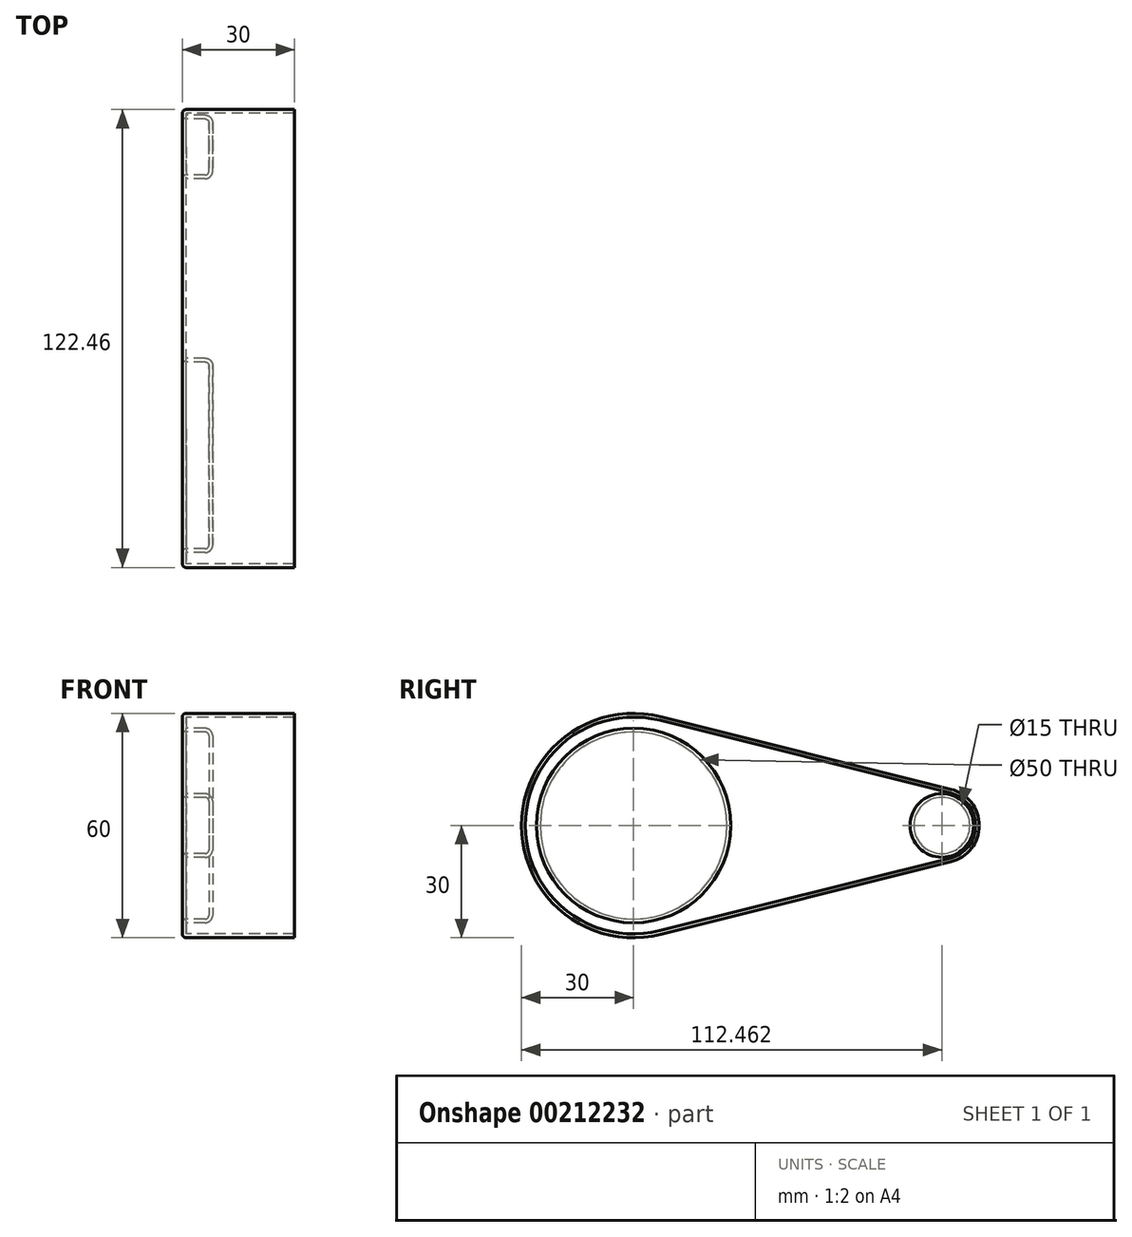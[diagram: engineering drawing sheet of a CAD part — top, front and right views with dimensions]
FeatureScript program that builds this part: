
annotation { "Feature Type Name" : "Feature", "Feature Type Description" : "" }
export const myFeature = defineFeature(function(context is Context, id is Id, definition is map)
    precondition{}
    {
        {
            var Q0;
            Q0=qCreatedBy(makeId("Right.planeOp"),FACE);
            var sketch = newSketch(context, id + "F0", { "sketchPlane" : qUnion([Q0])});
            skCircle(sketch, "E0", {"center": v(0, 0) * mm, "radius": 30 * mm});
            skCircle(sketch, "E1", {"center": v(82.46, 0) * mm, "radius": 10 * mm});
            skLineSegment(sketch, "E2", {"start": v(7.28, 29.1) * mm, "end": v(84.89, 9.7) * mm});
            skLineSegment(sketch, "E3", {"start": v(7.28, -29.1) * mm, "end": v(84.89, -9.7) * mm});
            skSolve(sketch);
        }
        {
            var Q0;
            {var subQ0=sQuery(id+"F0.wireOp",EDGE,"E0");var subQ1=makeQuery(id+"F0.imprint","INTERSECT",VERTEX,{"derivedFrom":[subQ0,sQuery(id+"F0.wireOp",EDGE,"E2")]});Q0=makeQuery(id+"F0.imprint","IMPRINT",FACE,{"disambiguationData":[TD([[makeQuery(id+"F0.imprint","IMPRINT",EDGE,{"disambiguationData":[TD([[subQ1,-1.0]])],"derivedFrom":subQ0}),1.0]])]});}
            var Q1;
            {var subQ0=sQuery(id+"F0.wireOp",EDGE,"E2");Q1=makeQuery(id+"F0.imprint","IMPRINT",FACE,{"disambiguationData":[TD([[makeQuery(id+"F0.imprint","IMPRINT",EDGE,{"derivedFrom":subQ0}),-1.0]])]});}
            var Q2;
            {var subQ0=sQuery(id+"F0.wireOp",EDGE,"E1");var subQ1=makeQuery(id+"F0.imprint","INTERSECT",VERTEX,{"derivedFrom":[subQ0,sQuery(id+"F0.wireOp",EDGE,"E2")]});Q2=makeQuery(id+"F0.imprint","IMPRINT",FACE,{"disambiguationData":[TD([[makeQuery(id+"F0.imprint","IMPRINT",EDGE,{"disambiguationData":[TD([[subQ1,-1.0]])],"derivedFrom":subQ0}),1.0]])]});}
            extrude(context, id + "F1", {"entities" : qUnion([Q0, Q1, Q2]), "depth" : 30 * mm});
        }
        {
            var Q0;
            Q0=makeQuery(id+"F1.opExtrude","CAP_FACE",FACE,{"disambiguationData":[OSD([sQuery(id+"F0.wireOp",EDGE,"E0"),sQuery(id+"F0.wireOp",EDGE,"E1"),sQuery(id+"F0.wireOp",EDGE,"E2"),sQuery(id+"F0.wireOp",EDGE,"E3")])],"isStart":true});
            var sketch = newSketch(context, id + "F2", { "sketchPlane" : qUnion([Q0])});
            skCircle(sketch, "E4", {"center": v(0, 0) * mm, "radius": 25 * mm});
            skCircle(sketch, "E5", {"center": v(-82.46, 0) * mm, "radius": 7.5 * mm});
            skSolve(sketch);
        }
        {
            var Q0;
            Q0=makeQuery(id+"F2.imprint","IMPRINT",FACE,{"disambiguationData":[TD([[makeQuery(id+"F2.imprint","IMPRINT",EDGE,{"derivedFrom":sQuery(id+"F2.wireOp",EDGE,"E4")}),1.0]])]});
            var Q1;
            Q1=makeQuery(id+"F2.imprint","IMPRINT",FACE,{"disambiguationData":[TD([[makeQuery(id+"F2.imprint","IMPRINT",EDGE,{"derivedFrom":sQuery(id+"F2.wireOp",EDGE,"E5")}),1.0]])]});
            var Q2;
            Q2=sQuery(id+"F2.wireOp",EDGE,"E4");
            var Q3;
            Q3=sQuery(id+"F2.wireOp",EDGE,"E5");
            extrude(context, id + "F3", {"entities" : qUnion([Q0, Q1]), "operationType" : NewBodyOperationType.REMOVE, "surfaceEntities" : qUnion([Q2, Q3]), "oppositeDirection" : true, "depth" : 7.1 * mm});
        }
        {
            var Q0;
            Q0=makeQuery(id+"F1.opExtrude","CAP_FACE",FACE,{"disambiguationData":[OSD([sQuery(id+"F0.wireOp",EDGE,"E0"),sQuery(id+"F0.wireOp",EDGE,"E1"),sQuery(id+"F0.wireOp",EDGE,"E2"),sQuery(id+"F0.wireOp",EDGE,"E3")])],"isStart":true});
            var Q1;
            Q1=makeQuery(id+"F3.boolean.opBoolean","COPY",FACE,{"derivedFrom":makeQuery(id+"F3.opExtrude","CAP_FACE",FACE,{"disambiguationData":[OSD([sQuery(id+"F2.wireOp",EDGE,"E4")])],"isStart":false})});
            var Q2;
            Q2=makeQuery(id+"F3.boolean.opBoolean","COPY",FACE,{"derivedFrom":makeQuery(id+"F3.opExtrude","CAP_FACE",FACE,{"disambiguationData":[OSD([sQuery(id+"F2.wireOp",EDGE,"E5")])],"isStart":false})});
            fillet(context, id + "F4", {"entities" : qUnion([Q0, Q1, Q2]), "radius" : 1 * mm, "tangentPropagation" : true, "allowEdgeOverflow" : false});
        }
        {
            var Q0;
            Q0=makeQuery(id+"F1.opExtrude","CAP_FACE",FACE,{"disambiguationData":[OSD([sQuery(id+"F0.wireOp",EDGE,"E0"),sQuery(id+"F0.wireOp",EDGE,"E1"),sQuery(id+"F0.wireOp",EDGE,"E2"),sQuery(id+"F0.wireOp",EDGE,"E3")])],"isStart":false});
            shell(context, id + "F5", {"entities" : qUnion([Q0]), "thickness" : 1 * mm});
        }
    });
